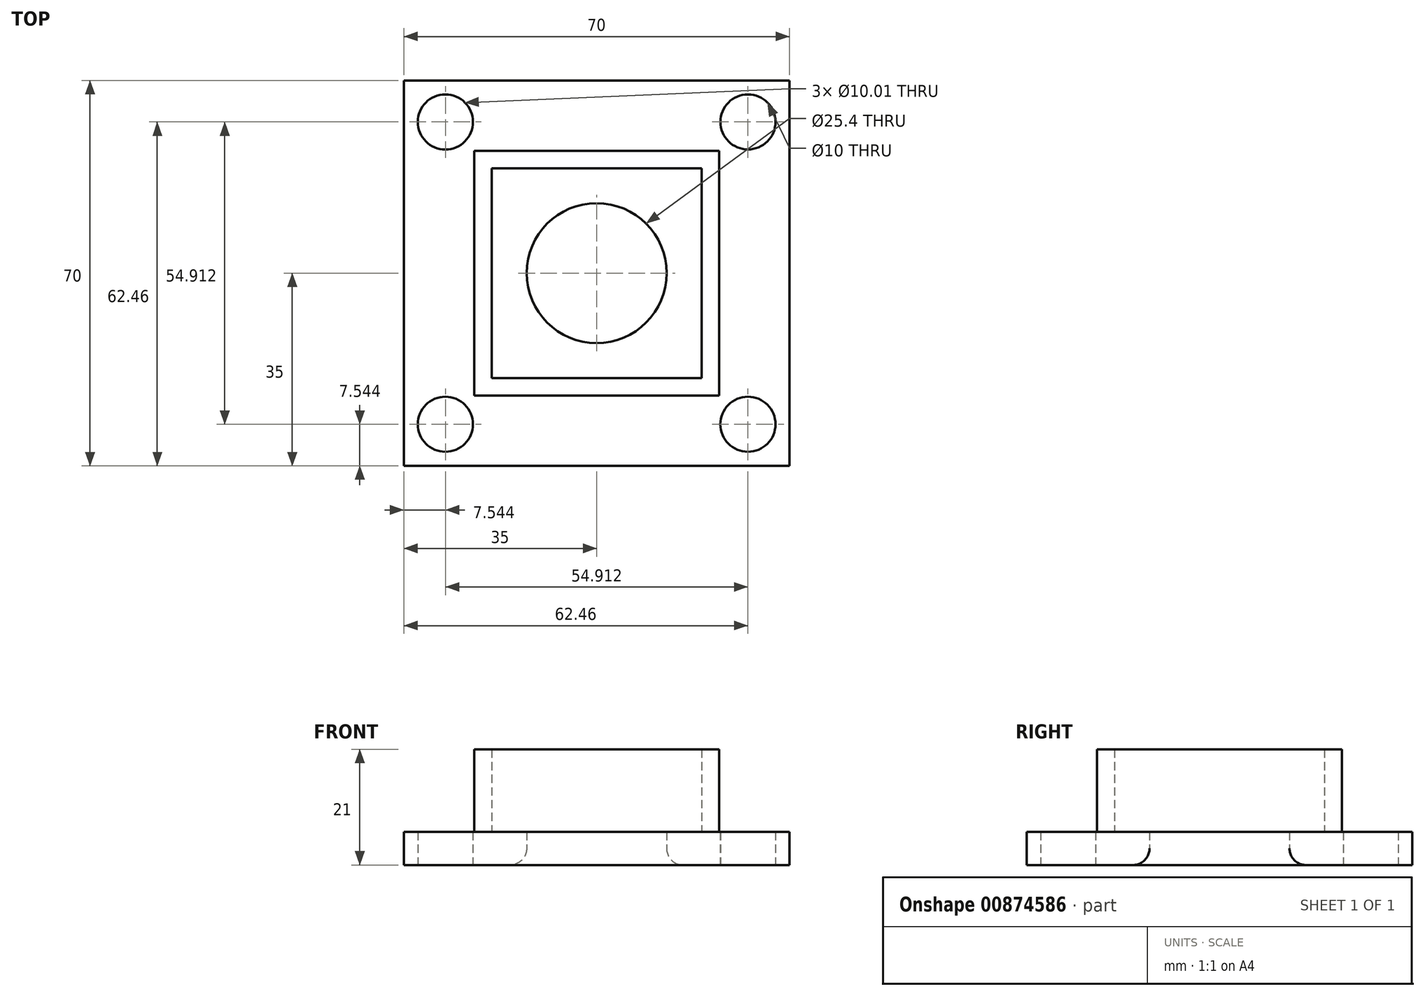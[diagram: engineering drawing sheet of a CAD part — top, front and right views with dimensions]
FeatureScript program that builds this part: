
annotation { "Feature Type Name" : "Feature", "Feature Type Description" : "" }
export const myFeature = defineFeature(function(context is Context, id is Id, definition is map)
    precondition{}
    {
        {
            var Q0;
            Q0=qCreatedBy(makeId("Top.planeOp"),FACE);
            var sketch = newSketch(context, id + "F0", { "sketchPlane" : qUnion([Q0])});
            skLineSegment(sketch, "E0.bottom", {"start": v(-35, 35) * mm, "end": v(35, 35) * mm});
            skLineSegment(sketch, "E0.top", {"start": v(-35, -35) * mm, "end": v(35, -35) * mm});
            skLineSegment(sketch, "E0.left", {"start": v(-35, 35) * mm, "end": v(-35, -35) * mm});
            skLineSegment(sketch, "E0.right", {"start": v(35, 35) * mm, "end": v(35, -35) * mm});
            skPoint(sketch, "E0.middle", {"position": v(0, 0) * mm});
            skCircle(sketch, "E1", {"center": v(0, 0) * mm, "radius": 12.7 * mm});
            skCircle(sketch, "E2", {"center": v(27.46, 27.46) * mm, "radius": 5 * mm});
            skCircle(sketch, "E3", {"center": v(27.46, -27.46) * mm, "radius": 5 * mm});
            skCircle(sketch, "E4", {"center": v(-27.46, 27.46) * mm, "radius": 5 * mm});
            skCircle(sketch, "E5", {"center": v(-27.46, -27.46) * mm, "radius": 5 * mm});
            skSolve(sketch);
        }
        {
            var Q0;
            Q0=makeQuery(id+"F0.imprint","IMPRINT",FACE,{"disambiguationData":[TD([[makeQuery(id+"F0.imprint","IMPRINT",EDGE,{"derivedFrom":sQuery(id+"F0.wireOp",EDGE,"E0.bottom")}),-1.0]])]});
            extrude(context, id + "F1", {"entities" : qUnion([Q0]), "depth" : 6 * mm, "offsetDistance" : 25.4 * mm});
        }
        {
            var Q0;
            Q0=makeQuery(id+"F1.opExtrude","CAP_EDGE",EDGE,{"disambiguationData":[OSD([sQuery(id+"F0.wireOp",EDGE,"E1")])],"isStart":true});
            fillet(context, id + "F2", {"entities" : qUnion([Q0]), "radius" : 3 * mm, "tangentPropagation" : true, "allowEdgeOverflow" : false});
        }
        {
            var Q0;
            Q0=makeQuery(id+"F1.opExtrude","CAP_FACE",FACE,{"disambiguationData":[OSD([sQuery(id+"F0.wireOp",EDGE,"E0.bottom"),sQuery(id+"F0.wireOp",EDGE,"E0.top"),sQuery(id+"F0.wireOp",EDGE,"E0.left"),sQuery(id+"F0.wireOp",EDGE,"E0.right"),sQuery(id+"F0.wireOp",EDGE,"E1"),sQuery(id+"F0.wireOp",EDGE,"E2"),sQuery(id+"F0.wireOp",EDGE,"E3"),sQuery(id+"F0.wireOp",EDGE,"E4"),sQuery(id+"F0.wireOp",EDGE,"E5")])],"isStart":false});
            var sketch = newSketch(context, id + "F3", { "sketchPlane" : qUnion([Q0])});
            skLineSegment(sketch, "E6.bottom", {"start": v(19.05, -19.05) * mm, "end": v(-19.05, -19.05) * mm});
            skLineSegment(sketch, "E6.top", {"start": v(19.05, 19.05) * mm, "end": v(-19.05, 19.05) * mm});
            skLineSegment(sketch, "E6.left", {"start": v(19.05, -19.05) * mm, "end": v(19.05, 19.05) * mm});
            skLineSegment(sketch, "E6.right", {"start": v(-19.05, -19.05) * mm, "end": v(-19.05, 19.05) * mm});
            skPoint(sketch, "E6.middle", {"position": v(0, 0) * mm});
            skLineSegment(sketch, "E7.bottom", {"start": v(22.22, -22.23) * mm, "end": v(-22.23, -22.23) * mm});
            skLineSegment(sketch, "E7.top", {"start": v(22.23, 22.23) * mm, "end": v(-22.22, 22.23) * mm});
            skLineSegment(sketch, "E7.left", {"start": v(22.22, -22.23) * mm, "end": v(22.23, 22.23) * mm});
            skLineSegment(sketch, "E7.right", {"start": v(-22.23, -22.23) * mm, "end": v(-22.22, 22.22) * mm});
            skSolve(sketch);
        }
        {
            var Q0;
            Q0=makeQuery(id+"F3.imprint","IMPRINT",FACE,{"disambiguationData":[TD([[makeQuery(id+"F3.imprint","IMPRINT",EDGE,{"derivedFrom":sQuery(id+"F3.wireOp",EDGE,"E6.bottom")}),1.0]])]});
            extrude(context, id + "F4", {"entities" : qUnion([Q0]), "operationType" : NewBodyOperationType.ADD, "depth" : 15 * mm, "offsetDistance" : 25.4 * mm});
        }
    });
